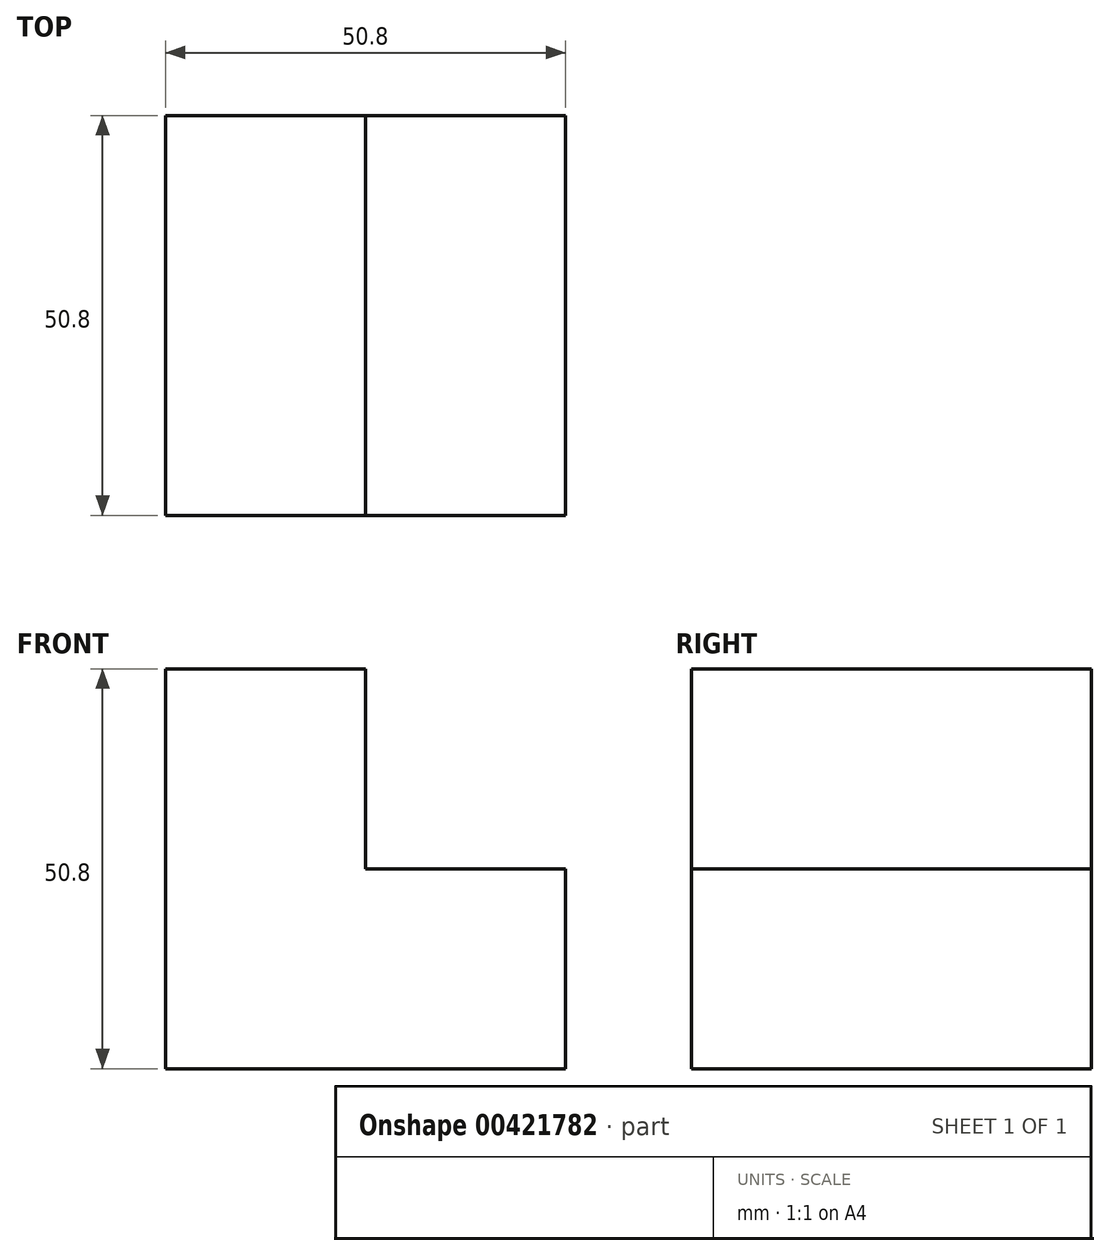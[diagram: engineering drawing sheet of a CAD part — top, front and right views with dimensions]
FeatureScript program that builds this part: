
annotation { "Feature Type Name" : "Feature", "Feature Type Description" : "" }
export const myFeature = defineFeature(function(context is Context, id is Id, definition is map)
    precondition{}
    {
        {
            var Q0;
            Q0=qCreatedBy(makeId("Front.planeOp"),FACE);
            var sketch = newSketch(context, id + "F0", { "sketchPlane" : qUnion([Q0])});
            skLineSegment(sketch, "E0", {"start": v(0, 0) * mm, "end": v(50.8, 0) * mm});
            skLineSegment(sketch, "E1", {"start": v(0, 0) * mm, "end": v(0, 50.8) * mm});
            skLineSegment(sketch, "E2", {"start": v(0, 50.8) * mm, "end": v(25.4, 50.8) * mm});
            skLineSegment(sketch, "E3", {"start": v(50.8, 0) * mm, "end": v(50.8, 25.4) * mm});
            skLineSegment(sketch, "E4", {"start": v(25.4, 50.8) * mm, "end": v(25.4, 25.4) * mm});
            skLineSegment(sketch, "E5", {"start": v(50.8, 25.4) * mm, "end": v(25.4, 25.4) * mm});
            skSolve(sketch);
        }
        {
            var Q0;
            Q0=makeQuery(id+"F0.imprint","IMPRINT",FACE,{"disambiguationData":[TD([[makeQuery(id+"F0.imprint","IMPRINT",EDGE,{"derivedFrom":sQuery(id+"F0.wireOp",EDGE,"E0")}),1.0]])]});
            extrude(context, id + "F1", {"entities" : qUnion([Q0]), "depth" : 50.8 * mm});
        }
    });
